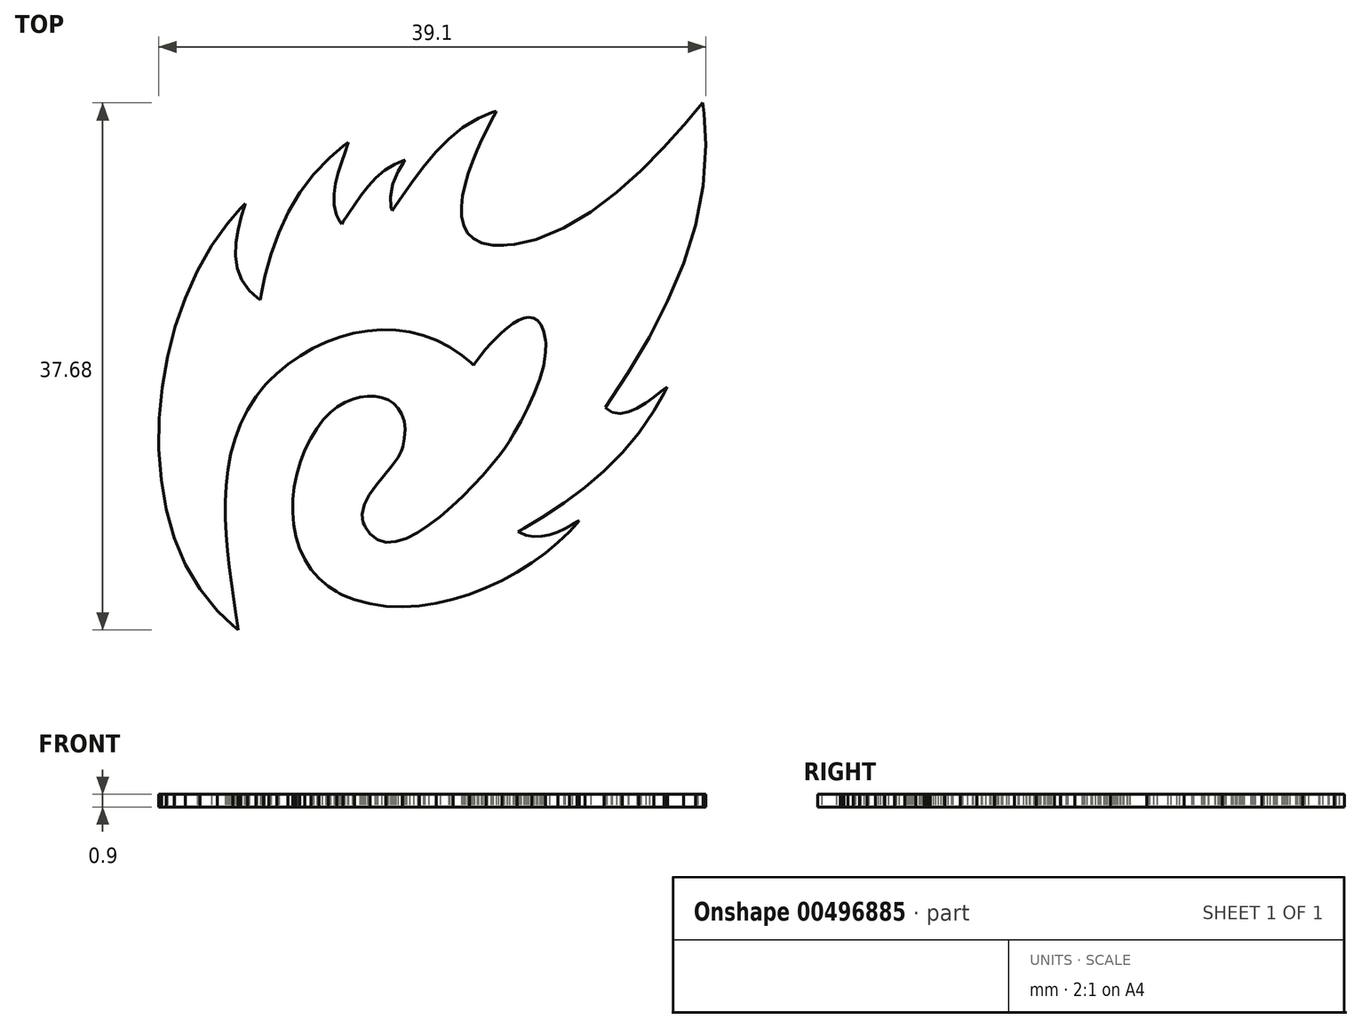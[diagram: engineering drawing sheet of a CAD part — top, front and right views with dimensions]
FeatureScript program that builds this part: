
annotation { "Feature Type Name" : "Feature", "Feature Type Description" : "" }
export const myFeature = defineFeature(function(context is Context, id is Id, definition is map)
    precondition{}
    {
        {
            var Q0;
            Q0=qCreatedBy(makeId("Top.planeOp"),FACE);
            var sketch = newSketch(context, id + "F0", { "sketchPlane" : qUnion([Q0])});
            skLineSegment(sketch, "E0", {"start": v(19.33, 18.84) * mm, "end": v(19.44, 18.1) * mm});
            skLineSegment(sketch, "E1", {"start": v(19.44, 18.1) * mm, "end": v(19.55, 15.84) * mm});
            skLineSegment(sketch, "E2", {"start": v(19.55, 15.84) * mm, "end": v(19.36, 12.93) * mm});
            skLineSegment(sketch, "E3", {"start": v(19.36, 12.93) * mm, "end": v(18.82, 10.1) * mm});
            skLineSegment(sketch, "E4", {"start": v(18.82, 10.1) * mm, "end": v(17.96, 7.36) * mm});
            skLineSegment(sketch, "E5", {"start": v(17.96, 7.36) * mm, "end": v(16.85, 4.69) * mm});
            skLineSegment(sketch, "E6", {"start": v(16.85, 4.69) * mm, "end": v(15.51, 2.09) * mm});
            skLineSegment(sketch, "E7", {"start": v(15.51, 2.09) * mm, "end": v(14.01, -0.45) * mm});
            skLineSegment(sketch, "E8", {"start": v(14.01, -0.45) * mm, "end": v(12.8, -2.31) * mm});
            skLineSegment(sketch, "E9", {"start": v(12.8, -2.31) * mm, "end": v(12.39, -2.92) * mm});
            skLineSegment(sketch, "E10", {"start": v(12.39, -2.92) * mm, "end": v(12.48, -3.04) * mm});
            skLineSegment(sketch, "E11", {"start": v(12.48, -3.04) * mm, "end": v(12.88, -3.29) * mm});
            skLineSegment(sketch, "E12", {"start": v(12.88, -3.29) * mm, "end": v(13.44, -3.38) * mm});
            skLineSegment(sketch, "E13", {"start": v(13.44, -3.38) * mm, "end": v(14.03, -3.26) * mm});
            skLineSegment(sketch, "E14", {"start": v(14.03, -3.26) * mm, "end": v(14.65, -2.99) * mm});
            skLineSegment(sketch, "E15", {"start": v(14.65, -2.99) * mm, "end": v(15.26, -2.61) * mm});
            skLineSegment(sketch, "E16", {"start": v(15.26, -2.61) * mm, "end": v(15.84, -2.2) * mm});
            skLineSegment(sketch, "E17", {"start": v(15.84, -2.2) * mm, "end": v(16.36, -1.8) * mm});
            skLineSegment(sketch, "E18", {"start": v(16.36, -1.8) * mm, "end": v(16.7, -1.54) * mm});
            skLineSegment(sketch, "E19", {"start": v(16.7, -1.54) * mm, "end": v(16.8, -1.46) * mm});
            skLineSegment(sketch, "E20", {"start": v(16.8, -1.46) * mm, "end": v(16.59, -1.9) * mm});
            skLineSegment(sketch, "E21", {"start": v(16.59, -1.9) * mm, "end": v(15.84, -3.2) * mm});
            skLineSegment(sketch, "E22", {"start": v(15.84, -3.2) * mm, "end": v(14.76, -4.76) * mm});
            skLineSegment(sketch, "E23", {"start": v(14.76, -4.76) * mm, "end": v(13.58, -6.18) * mm});
            skLineSegment(sketch, "E24", {"start": v(13.58, -6.18) * mm, "end": v(12.3, -7.47) * mm});
            skLineSegment(sketch, "E25", {"start": v(12.3, -7.47) * mm, "end": v(10.92, -8.65) * mm});
            skLineSegment(sketch, "E26", {"start": v(10.92, -8.65) * mm, "end": v(9.43, -9.76) * mm});
            skLineSegment(sketch, "E27", {"start": v(9.43, -9.76) * mm, "end": v(7.84, -10.8) * mm});
            skLineSegment(sketch, "E28", {"start": v(7.84, -10.8) * mm, "end": v(6.57, -11.58) * mm});
            skLineSegment(sketch, "E29", {"start": v(6.57, -11.58) * mm, "end": v(6.15, -11.82) * mm});
            skLineSegment(sketch, "E30", {"start": v(6.15, -11.82) * mm, "end": v(6.28, -11.9) * mm});
            skLineSegment(sketch, "E31", {"start": v(6.28, -11.9) * mm, "end": v(6.7, -12.06) * mm});
            skLineSegment(sketch, "E32", {"start": v(6.7, -12.06) * mm, "end": v(7.27, -12.17) * mm});
            skLineSegment(sketch, "E33", {"start": v(7.27, -12.17) * mm, "end": v(7.83, -12.15) * mm});
            skLineSegment(sketch, "E34", {"start": v(7.83, -12.15) * mm, "end": v(8.4, -12.03) * mm});
            skLineSegment(sketch, "E35", {"start": v(8.4, -12.03) * mm, "end": v(8.95, -11.84) * mm});
            skLineSegment(sketch, "E36", {"start": v(8.95, -11.84) * mm, "end": v(9.5, -11.59) * mm});
            skLineSegment(sketch, "E37", {"start": v(9.5, -11.59) * mm, "end": v(10.02, -11.3) * mm});
            skLineSegment(sketch, "E38", {"start": v(10.02, -11.3) * mm, "end": v(10.4, -11.09) * mm});
            skLineSegment(sketch, "E39", {"start": v(10.4, -11.09) * mm, "end": v(10.52, -11.02) * mm});
            skLineSegment(sketch, "E40", {"start": v(10.52, -11.02) * mm, "end": v(10.35, -11.22) * mm});
            skLineSegment(sketch, "E41", {"start": v(10.35, -11.22) * mm, "end": v(9.8, -11.82) * mm});
            skLineSegment(sketch, "E42", {"start": v(9.8, -11.82) * mm, "end": v(8.99, -12.6) * mm});
            skLineSegment(sketch, "E43", {"start": v(8.99, -12.6) * mm, "end": v(8.09, -13.34) * mm});
            skLineSegment(sketch, "E44", {"start": v(8.09, -13.34) * mm, "end": v(7.12, -14.04) * mm});
            skLineSegment(sketch, "E45", {"start": v(7.12, -14.04) * mm, "end": v(6.08, -14.7) * mm});
            skLineSegment(sketch, "E46", {"start": v(6.08, -14.7) * mm, "end": v(4.99, -15.3) * mm});
            skLineSegment(sketch, "E47", {"start": v(4.99, -15.3) * mm, "end": v(3.85, -15.83) * mm});
            skLineSegment(sketch, "E48", {"start": v(3.85, -15.83) * mm, "end": v(2.68, -16.29) * mm});
            skLineSegment(sketch, "E49", {"start": v(2.68, -16.29) * mm, "end": v(1.5, -16.66) * mm});
            skLineSegment(sketch, "E50", {"start": v(1.5, -16.66) * mm, "end": v(0.3, -16.94) * mm});
            skLineSegment(sketch, "E51", {"start": v(0.3, -16.94) * mm, "end": v(-0.91, -17.12) * mm});
            skLineSegment(sketch, "E52", {"start": v(-0.91, -17.12) * mm, "end": v(-2.11, -17.2) * mm});
            skLineSegment(sketch, "E53", {"start": v(-2.11, -17.2) * mm, "end": v(-3.3, -17.15) * mm});
            skLineSegment(sketch, "E54", {"start": v(-3.3, -17.15) * mm, "end": v(-4.44, -16.98) * mm});
            skLineSegment(sketch, "E55", {"start": v(-4.44, -16.98) * mm, "end": v(-5.56, -16.67) * mm});
            skLineSegment(sketch, "E56", {"start": v(-5.56, -16.67) * mm, "end": v(-6.37, -16.35) * mm});
            skLineSegment(sketch, "E57", {"start": v(-6.37, -16.35) * mm, "end": v(-6.62, -16.22) * mm});
            skLineSegment(sketch, "E58", {"start": v(-6.62, -16.22) * mm, "end": v(-6.83, -16.11) * mm});
            skLineSegment(sketch, "E59", {"start": v(-6.83, -16.11) * mm, "end": v(-7.41, -15.74) * mm});
            skLineSegment(sketch, "E60", {"start": v(-7.41, -15.74) * mm, "end": v(-8.1, -15.17) * mm});
            skLineSegment(sketch, "E61", {"start": v(-8.1, -15.17) * mm, "end": v(-8.66, -14.51) * mm});
            skLineSegment(sketch, "E62", {"start": v(-8.66, -14.51) * mm, "end": v(-9.12, -13.79) * mm});
            skLineSegment(sketch, "E63", {"start": v(-9.12, -13.79) * mm, "end": v(-9.48, -13) * mm});
            skLineSegment(sketch, "E64", {"start": v(-9.48, -13) * mm, "end": v(-9.74, -12.18) * mm});
            skLineSegment(sketch, "E65", {"start": v(-9.74, -12.18) * mm, "end": v(-9.9, -11.3) * mm});
            skLineSegment(sketch, "E66", {"start": v(-9.9, -11.3) * mm, "end": v(-9.97, -10.42) * mm});
            skLineSegment(sketch, "E67", {"start": v(-9.97, -10.42) * mm, "end": v(-9.96, -9.51) * mm});
            skLineSegment(sketch, "E68", {"start": v(-9.96, -9.51) * mm, "end": v(-9.86, -8.6) * mm});
            skLineSegment(sketch, "E69", {"start": v(-9.86, -8.6) * mm, "end": v(-9.68, -7.7) * mm});
            skLineSegment(sketch, "E70", {"start": v(-9.68, -7.7) * mm, "end": v(-9.43, -6.83) * mm});
            skLineSegment(sketch, "E71", {"start": v(-9.43, -6.83) * mm, "end": v(-9.1, -5.99) * mm});
            skLineSegment(sketch, "E72", {"start": v(-9.1, -5.99) * mm, "end": v(-8.71, -5.19) * mm});
            skLineSegment(sketch, "E73", {"start": v(-8.71, -5.19) * mm, "end": v(-8.25, -4.44) * mm});
            skLineSegment(sketch, "E74", {"start": v(-8.25, -4.44) * mm, "end": v(-7.87, -3.93) * mm});
            skLineSegment(sketch, "E75", {"start": v(-7.87, -3.93) * mm, "end": v(-7.74, -3.76) * mm});
            skLineSegment(sketch, "E76", {"start": v(-7.74, -3.76) * mm, "end": v(-7.63, -3.64) * mm});
            skLineSegment(sketch, "E77", {"start": v(-7.63, -3.64) * mm, "end": v(-7.28, -3.3) * mm});
            skLineSegment(sketch, "E78", {"start": v(-7.28, -3.3) * mm, "end": v(-6.78, -2.9) * mm});
            skLineSegment(sketch, "E79", {"start": v(-6.78, -2.9) * mm, "end": v(-6.25, -2.59) * mm});
            skLineSegment(sketch, "E80", {"start": v(-6.25, -2.59) * mm, "end": v(-5.7, -2.35) * mm});
            skLineSegment(sketch, "E81", {"start": v(-5.7, -2.35) * mm, "end": v(-5.16, -2.2) * mm});
            skLineSegment(sketch, "E82", {"start": v(-5.16, -2.2) * mm, "end": v(-4.62, -2.13) * mm});
            skLineSegment(sketch, "E83", {"start": v(-4.62, -2.13) * mm, "end": v(-4.1, -2.14) * mm});
            skLineSegment(sketch, "E84", {"start": v(-4.1, -2.14) * mm, "end": v(-3.6, -2.23) * mm});
            skLineSegment(sketch, "E85", {"start": v(-3.6, -2.23) * mm, "end": v(-3.15, -2.4) * mm});
            skLineSegment(sketch, "E86", {"start": v(-3.15, -2.4) * mm, "end": v(-2.76, -2.65) * mm});
            skLineSegment(sketch, "E87", {"start": v(-2.76, -2.65) * mm, "end": v(-2.43, -2.99) * mm});
            skLineSegment(sketch, "E88", {"start": v(-2.43, -2.99) * mm, "end": v(-2.17, -3.4) * mm});
            skLineSegment(sketch, "E89", {"start": v(-2.17, -3.4) * mm, "end": v(-2, -3.9) * mm});
            skLineSegment(sketch, "E90", {"start": v(-2, -3.9) * mm, "end": v(-1.94, -4.5) * mm});
            skLineSegment(sketch, "E91", {"start": v(-1.94, -4.5) * mm, "end": v(-2, -5.16) * mm});
            skLineSegment(sketch, "E92", {"start": v(-2, -5.16) * mm, "end": v(-2.1, -5.73) * mm});
            skLineSegment(sketch, "E93", {"start": v(-2.1, -5.73) * mm, "end": v(-2.16, -5.91) * mm});
            skLineSegment(sketch, "E94", {"start": v(-2.16, -5.91) * mm, "end": v(-2.21, -6.07) * mm});
            skLineSegment(sketch, "E95", {"start": v(-2.21, -6.07) * mm, "end": v(-2.45, -6.52) * mm});
            skLineSegment(sketch, "E96", {"start": v(-2.45, -6.52) * mm, "end": v(-2.9, -7.16) * mm});
            skLineSegment(sketch, "E97", {"start": v(-2.9, -7.16) * mm, "end": v(-3.45, -7.81) * mm});
            skLineSegment(sketch, "E98", {"start": v(-3.45, -7.81) * mm, "end": v(-4, -8.49) * mm});
            skLineSegment(sketch, "E99", {"start": v(-4, -8.49) * mm, "end": v(-4.5, -9.18) * mm});
            skLineSegment(sketch, "E100", {"start": v(-4.5, -9.18) * mm, "end": v(-4.86, -9.88) * mm});
            skLineSegment(sketch, "E101", {"start": v(-4.86, -9.88) * mm, "end": v(-5, -10.59) * mm});
            skLineSegment(sketch, "E102", {"start": v(-5, -10.59) * mm, "end": v(-4.94, -11.14) * mm});
            skLineSegment(sketch, "E103", {"start": v(-4.94, -11.14) * mm, "end": v(-4.87, -11.3) * mm});
            skLineSegment(sketch, "E104", {"start": v(-4.87, -11.3) * mm, "end": v(-4.79, -11.48) * mm});
            skLineSegment(sketch, "E105", {"start": v(-4.79, -11.48) * mm, "end": v(-4.44, -11.99) * mm});
            skLineSegment(sketch, "E106", {"start": v(-4.44, -11.99) * mm, "end": v(-3.91, -12.4) * mm});
            skLineSegment(sketch, "E107", {"start": v(-3.91, -12.4) * mm, "end": v(-3.29, -12.57) * mm});
            skLineSegment(sketch, "E108", {"start": v(-3.29, -12.57) * mm, "end": v(-2.6, -12.52) * mm});
            skLineSegment(sketch, "E109", {"start": v(-2.6, -12.52) * mm, "end": v(-1.84, -12.28) * mm});
            skLineSegment(sketch, "E110", {"start": v(-1.84, -12.28) * mm, "end": v(-1.05, -11.88) * mm});
            skLineSegment(sketch, "E111", {"start": v(-1.05, -11.88) * mm, "end": v(-0.24, -11.36) * mm});
            skLineSegment(sketch, "E112", {"start": v(-0.24, -11.36) * mm, "end": v(0.59, -10.73) * mm});
            skLineSegment(sketch, "E113", {"start": v(0.59, -10.73) * mm, "end": v(1.4, -10.02) * mm});
            skLineSegment(sketch, "E114", {"start": v(1.4, -10.02) * mm, "end": v(2.19, -9.28) * mm});
            skLineSegment(sketch, "E115", {"start": v(2.19, -9.28) * mm, "end": v(2.93, -8.52) * mm});
            skLineSegment(sketch, "E116", {"start": v(2.93, -8.52) * mm, "end": v(3.61, -7.77) * mm});
            skLineSegment(sketch, "E117", {"start": v(3.61, -7.77) * mm, "end": v(4.22, -7.07) * mm});
            skLineSegment(sketch, "E118", {"start": v(4.22, -7.07) * mm, "end": v(4.73, -6.44) * mm});
            skLineSegment(sketch, "E119", {"start": v(4.73, -6.44) * mm, "end": v(5.13, -5.92) * mm});
            skLineSegment(sketch, "E120", {"start": v(5.13, -5.92) * mm, "end": v(5.34, -5.62) * mm});
            skLineSegment(sketch, "E121", {"start": v(5.34, -5.62) * mm, "end": v(5.4, -5.52) * mm});
            skLineSegment(sketch, "E122", {"start": v(5.4, -5.52) * mm, "end": v(5.52, -5.34) * mm});
            skLineSegment(sketch, "E123", {"start": v(5.52, -5.34) * mm, "end": v(5.86, -4.78) * mm});
            skLineSegment(sketch, "E124", {"start": v(5.86, -4.78) * mm, "end": v(6.35, -3.92) * mm});
            skLineSegment(sketch, "E125", {"start": v(6.35, -3.92) * mm, "end": v(6.84, -2.97) * mm});
            skLineSegment(sketch, "E126", {"start": v(6.84, -2.97) * mm, "end": v(7.29, -1.97) * mm});
            skLineSegment(sketch, "E127", {"start": v(7.29, -1.97) * mm, "end": v(7.68, -0.95) * mm});
            skLineSegment(sketch, "E128", {"start": v(7.68, -0.95) * mm, "end": v(7.96, 0.06) * mm});
            skLineSegment(sketch, "E129", {"start": v(7.96, 0.06) * mm, "end": v(8.12, 1.01) * mm});
            skLineSegment(sketch, "E130", {"start": v(8.12, 1.01) * mm, "end": v(8.13, 1.66) * mm});
            skLineSegment(sketch, "E131", {"start": v(8.13, 1.66) * mm, "end": v(8.1, 1.87) * mm});
            skLineSegment(sketch, "E132", {"start": v(8.1, 1.87) * mm, "end": v(8.08, 2.03) * mm});
            skLineSegment(sketch, "E133", {"start": v(8.08, 2.03) * mm, "end": v(7.97, 2.5) * mm});
            skLineSegment(sketch, "E134", {"start": v(7.97, 2.5) * mm, "end": v(7.77, 2.97) * mm});
            skLineSegment(sketch, "E135", {"start": v(7.77, 2.97) * mm, "end": v(7.53, 3.28) * mm});
            skLineSegment(sketch, "E136", {"start": v(7.53, 3.28) * mm, "end": v(7.23, 3.46) * mm});
            skLineSegment(sketch, "E137", {"start": v(7.23, 3.46) * mm, "end": v(6.9, 3.5) * mm});
            skLineSegment(sketch, "E138", {"start": v(6.9, 3.5) * mm, "end": v(6.55, 3.45) * mm});
            skLineSegment(sketch, "E139", {"start": v(6.55, 3.45) * mm, "end": v(6.17, 3.3) * mm});
            skLineSegment(sketch, "E140", {"start": v(6.17, 3.3) * mm, "end": v(5.77, 3.06) * mm});
            skLineSegment(sketch, "E141", {"start": v(5.77, 3.06) * mm, "end": v(5.36, 2.77) * mm});
            skLineSegment(sketch, "E142", {"start": v(5.36, 2.77) * mm, "end": v(4.96, 2.42) * mm});
            skLineSegment(sketch, "E143", {"start": v(4.96, 2.42) * mm, "end": v(4.57, 2.03) * mm});
            skLineSegment(sketch, "E144", {"start": v(4.57, 2.03) * mm, "end": v(4.19, 1.63) * mm});
            skLineSegment(sketch, "E145", {"start": v(4.19, 1.63) * mm, "end": v(3.83, 1.21) * mm});
            skLineSegment(sketch, "E146", {"start": v(3.83, 1.21) * mm, "end": v(3.5, 0.8) * mm});
            skLineSegment(sketch, "E147", {"start": v(3.5, 0.8) * mm, "end": v(3.21, 0.43) * mm});
            skLineSegment(sketch, "E148", {"start": v(3.21, 0.43) * mm, "end": v(3.03, 0.17) * mm});
            skLineSegment(sketch, "E149", {"start": v(3.03, 0.17) * mm, "end": v(2.97, 0.08) * mm});
            skLineSegment(sketch, "E150", {"start": v(2.97, 0.08) * mm, "end": v(2.77, 0.27) * mm});
            skLineSegment(sketch, "E151", {"start": v(2.77, 0.27) * mm, "end": v(2.14, 0.8) * mm});
            skLineSegment(sketch, "E152", {"start": v(2.14, 0.8) * mm, "end": v(1.25, 1.4) * mm});
            skLineSegment(sketch, "E153", {"start": v(1.25, 1.4) * mm, "end": v(0.33, 1.86) * mm});
            skLineSegment(sketch, "E154", {"start": v(0.33, 1.86) * mm, "end": v(-0.63, 2.22) * mm});
            skLineSegment(sketch, "E155", {"start": v(-0.63, 2.22) * mm, "end": v(-1.6, 2.46) * mm});
            skLineSegment(sketch, "E156", {"start": v(-1.6, 2.46) * mm, "end": v(-2.6, 2.59) * mm});
            skLineSegment(sketch, "E157", {"start": v(-2.6, 2.59) * mm, "end": v(-3.62, 2.61) * mm});
            skLineSegment(sketch, "E158", {"start": v(-3.62, 2.61) * mm, "end": v(-4.63, 2.54) * mm});
            skLineSegment(sketch, "E159", {"start": v(-4.63, 2.54) * mm, "end": v(-5.63, 2.36) * mm});
            skLineSegment(sketch, "E160", {"start": v(-5.63, 2.36) * mm, "end": v(-6.62, 2.1) * mm});
            skLineSegment(sketch, "E161", {"start": v(-6.62, 2.1) * mm, "end": v(-7.6, 1.74) * mm});
            skLineSegment(sketch, "E162", {"start": v(-7.6, 1.74) * mm, "end": v(-8.53, 1.3) * mm});
            skLineSegment(sketch, "E163", {"start": v(-8.53, 1.3) * mm, "end": v(-9.44, 0.77) * mm});
            skLineSegment(sketch, "E164", {"start": v(-9.44, 0.77) * mm, "end": v(-10.3, 0.16) * mm});
            skLineSegment(sketch, "E165", {"start": v(-10.3, 0.16) * mm, "end": v(-11.1, -0.52) * mm});
            skLineSegment(sketch, "E166", {"start": v(-11.1, -0.52) * mm, "end": v(-11.68, -1.07) * mm});
            skLineSegment(sketch, "E167", {"start": v(-11.68, -1.07) * mm, "end": v(-11.86, -1.26) * mm});
            skLineSegment(sketch, "E168", {"start": v(-11.86, -1.26) * mm, "end": v(-12.06, -1.48) * mm});
            skLineSegment(sketch, "E169", {"start": v(-12.06, -1.48) * mm, "end": v(-12.6, -2.17) * mm});
            skLineSegment(sketch, "E170", {"start": v(-12.6, -2.17) * mm, "end": v(-13.21, -3.13) * mm});
            skLineSegment(sketch, "E171", {"start": v(-13.21, -3.13) * mm, "end": v(-13.71, -4.14) * mm});
            skLineSegment(sketch, "E172", {"start": v(-13.71, -4.14) * mm, "end": v(-14.1, -5.19) * mm});
            skLineSegment(sketch, "E173", {"start": v(-14.1, -5.19) * mm, "end": v(-14.4, -6.27) * mm});
            skLineSegment(sketch, "E174", {"start": v(-14.4, -6.27) * mm, "end": v(-14.6, -7.39) * mm});
            skLineSegment(sketch, "E175", {"start": v(-14.6, -7.39) * mm, "end": v(-14.73, -8.53) * mm});
            skLineSegment(sketch, "E176", {"start": v(-14.73, -8.53) * mm, "end": v(-14.79, -9.68) * mm});
            skLineSegment(sketch, "E177", {"start": v(-14.79, -9.68) * mm, "end": v(-14.79, -10.85) * mm});
            skLineSegment(sketch, "E178", {"start": v(-14.79, -10.85) * mm, "end": v(-14.73, -12.02) * mm});
            skLineSegment(sketch, "E179", {"start": v(-14.73, -12.02) * mm, "end": v(-14.64, -13.2) * mm});
            skLineSegment(sketch, "E180", {"start": v(-14.64, -13.2) * mm, "end": v(-14.51, -14.36) * mm});
            skLineSegment(sketch, "E181", {"start": v(-14.51, -14.36) * mm, "end": v(-14.36, -15.51) * mm});
            skLineSegment(sketch, "E182", {"start": v(-14.36, -15.51) * mm, "end": v(-14.2, -16.65) * mm});
            skLineSegment(sketch, "E183", {"start": v(-14.2, -16.65) * mm, "end": v(-14.03, -17.76) * mm});
            skLineSegment(sketch, "E184", {"start": v(-14.03, -17.76) * mm, "end": v(-13.9, -18.57) * mm});
            skLineSegment(sketch, "E185", {"start": v(-13.9, -18.57) * mm, "end": v(-13.86, -18.84) * mm});
            skLineSegment(sketch, "E186", {"start": v(-13.86, -18.84) * mm, "end": v(-14.26, -18.53) * mm});
            skLineSegment(sketch, "E187", {"start": v(-14.26, -18.53) * mm, "end": v(-15.36, -17.48) * mm});
            skLineSegment(sketch, "E188", {"start": v(-15.36, -17.48) * mm, "end": v(-16.61, -15.91) * mm});
            skLineSegment(sketch, "E189", {"start": v(-16.61, -15.91) * mm, "end": v(-17.64, -14.16) * mm});
            skLineSegment(sketch, "E190", {"start": v(-17.64, -14.16) * mm, "end": v(-18.43, -12.26) * mm});
            skLineSegment(sketch, "E191", {"start": v(-18.43, -12.26) * mm, "end": v(-19.01, -10.23) * mm});
            skLineSegment(sketch, "E192", {"start": v(-19.01, -10.23) * mm, "end": v(-19.38, -8.11) * mm});
            skLineSegment(sketch, "E193", {"start": v(-19.38, -8.11) * mm, "end": v(-19.55, -5.93) * mm});
            skLineSegment(sketch, "E194", {"start": v(-19.55, -5.93) * mm, "end": v(-19.52, -3.72) * mm});
            skLineSegment(sketch, "E195", {"start": v(-19.52, -3.72) * mm, "end": v(-19.31, -1.5) * mm});
            skLineSegment(sketch, "E196", {"start": v(-19.31, -1.5) * mm, "end": v(-18.93, 0.7) * mm});
            skLineSegment(sketch, "E197", {"start": v(-18.93, 0.7) * mm, "end": v(-18.37, 2.83) * mm});
            skLineSegment(sketch, "E198", {"start": v(-18.37, 2.83) * mm, "end": v(-17.66, 4.89) * mm});
            skLineSegment(sketch, "E199", {"start": v(-17.66, 4.89) * mm, "end": v(-16.8, 6.82) * mm});
            skLineSegment(sketch, "E200", {"start": v(-16.8, 6.82) * mm, "end": v(-15.78, 8.61) * mm});
            skLineSegment(sketch, "E201", {"start": v(-15.78, 8.61) * mm, "end": v(-14.64, 10.23) * mm});
            skLineSegment(sketch, "E202", {"start": v(-14.64, 10.23) * mm, "end": v(-13.7, 11.3) * mm});
            skLineSegment(sketch, "E203", {"start": v(-13.7, 11.3) * mm, "end": v(-13.37, 11.64) * mm});
            skLineSegment(sketch, "E204", {"start": v(-13.37, 11.64) * mm, "end": v(-13.44, 11.41) * mm});
            skLineSegment(sketch, "E205", {"start": v(-13.44, 11.41) * mm, "end": v(-13.65, 10.72) * mm});
            skLineSegment(sketch, "E206", {"start": v(-13.65, 10.72) * mm, "end": v(-13.87, 9.78) * mm});
            skLineSegment(sketch, "E207", {"start": v(-13.87, 9.78) * mm, "end": v(-14.02, 8.84) * mm});
            skLineSegment(sketch, "E208", {"start": v(-14.02, 8.84) * mm, "end": v(-14.05, 7.9) * mm});
            skLineSegment(sketch, "E209", {"start": v(-14.05, 7.9) * mm, "end": v(-13.92, 7.02) * mm});
            skLineSegment(sketch, "E210", {"start": v(-13.92, 7.02) * mm, "end": v(-13.6, 6.18) * mm});
            skLineSegment(sketch, "E211", {"start": v(-13.6, 6.18) * mm, "end": v(-13.07, 5.42) * mm});
            skLineSegment(sketch, "E212", {"start": v(-13.07, 5.42) * mm, "end": v(-12.5, 4.9) * mm});
            skLineSegment(sketch, "E213", {"start": v(-12.5, 4.9) * mm, "end": v(-12.28, 4.76) * mm});
            skLineSegment(sketch, "E214", {"start": v(-12.28, 4.76) * mm, "end": v(-12.21, 5.18) * mm});
            skLineSegment(sketch, "E215", {"start": v(-12.21, 5.18) * mm, "end": v(-11.95, 6.42) * mm});
            skLineSegment(sketch, "E216", {"start": v(-11.95, 6.42) * mm, "end": v(-11.52, 8.03) * mm});
            skLineSegment(sketch, "E217", {"start": v(-11.52, 8.03) * mm, "end": v(-10.96, 9.58) * mm});
            skLineSegment(sketch, "E218", {"start": v(-10.96, 9.58) * mm, "end": v(-10.28, 11.05) * mm});
            skLineSegment(sketch, "E219", {"start": v(-10.28, 11.05) * mm, "end": v(-9.45, 12.44) * mm});
            skLineSegment(sketch, "E220", {"start": v(-9.45, 12.44) * mm, "end": v(-8.47, 13.74) * mm});
            skLineSegment(sketch, "E221", {"start": v(-8.47, 13.74) * mm, "end": v(-7.32, 14.93) * mm});
            skLineSegment(sketch, "E222", {"start": v(-7.32, 14.93) * mm, "end": v(-6.33, 15.76) * mm});
            skLineSegment(sketch, "E223", {"start": v(-6.33, 15.76) * mm, "end": v(-5.99, 16) * mm});
            skLineSegment(sketch, "E224", {"start": v(-5.99, 16) * mm, "end": v(-6.05, 15.84) * mm});
            skLineSegment(sketch, "E225", {"start": v(-6.05, 15.84) * mm, "end": v(-6.23, 15.33) * mm});
            skLineSegment(sketch, "E226", {"start": v(-6.23, 15.33) * mm, "end": v(-6.49, 14.6) * mm});
            skLineSegment(sketch, "E227", {"start": v(-6.49, 14.6) * mm, "end": v(-6.73, 13.85) * mm});
            skLineSegment(sketch, "E228", {"start": v(-6.73, 13.85) * mm, "end": v(-6.92, 13.07) * mm});
            skLineSegment(sketch, "E229", {"start": v(-6.92, 13.07) * mm, "end": v(-7.02, 12.3) * mm});
            skLineSegment(sketch, "E230", {"start": v(-7.02, 12.3) * mm, "end": v(-7, 11.56) * mm});
            skLineSegment(sketch, "E231", {"start": v(-7, 11.56) * mm, "end": v(-6.84, 10.84) * mm});
            skLineSegment(sketch, "E232", {"start": v(-6.84, 10.84) * mm, "end": v(-6.6, 10.33) * mm});
            skLineSegment(sketch, "E233", {"start": v(-6.6, 10.33) * mm, "end": v(-6.49, 10.18) * mm});
            skLineSegment(sketch, "E234", {"start": v(-6.49, 10.18) * mm, "end": v(-6.37, 10.35) * mm});
            skLineSegment(sketch, "E235", {"start": v(-6.37, 10.35) * mm, "end": v(-6.03, 10.86) * mm});
            skLineSegment(sketch, "E236", {"start": v(-6.03, 10.86) * mm, "end": v(-5.56, 11.55) * mm});
            skLineSegment(sketch, "E237", {"start": v(-5.56, 11.55) * mm, "end": v(-5.08, 12.23) * mm});
            skLineSegment(sketch, "E238", {"start": v(-5.08, 12.23) * mm, "end": v(-4.57, 12.89) * mm});
            skLineSegment(sketch, "E239", {"start": v(-4.57, 12.89) * mm, "end": v(-4.01, 13.5) * mm});
            skLineSegment(sketch, "E240", {"start": v(-4.01, 13.5) * mm, "end": v(-3.4, 14.02) * mm});
            skLineSegment(sketch, "E241", {"start": v(-3.4, 14.02) * mm, "end": v(-2.7, 14.45) * mm});
            skLineSegment(sketch, "E242", {"start": v(-2.7, 14.45) * mm, "end": v(-2.12, 14.7) * mm});
            skLineSegment(sketch, "E243", {"start": v(-2.12, 14.7) * mm, "end": v(-1.92, 14.76) * mm});
            skLineSegment(sketch, "E244", {"start": v(-1.92, 14.76) * mm, "end": v(-2.07, 14.56) * mm});
            skLineSegment(sketch, "E245", {"start": v(-2.07, 14.56) * mm, "end": v(-2.45, 13.93) * mm});
            skLineSegment(sketch, "E246", {"start": v(-2.45, 13.93) * mm, "end": v(-2.82, 13.04) * mm});
            skLineSegment(sketch, "E247", {"start": v(-2.82, 13.04) * mm, "end": v(-2.98, 12.11) * mm});
            skLineSegment(sketch, "E248", {"start": v(-2.98, 12.11) * mm, "end": v(-2.93, 11.38) * mm});
            skLineSegment(sketch, "E249", {"start": v(-2.93, 11.38) * mm, "end": v(-2.87, 11.14) * mm});
            skLineSegment(sketch, "E250", {"start": v(-2.87, 11.14) * mm, "end": v(-2.67, 11.41) * mm});
            skLineSegment(sketch, "E251", {"start": v(-2.67, 11.41) * mm, "end": v(-2.08, 12.24) * mm});
            skLineSegment(sketch, "E252", {"start": v(-2.08, 12.24) * mm, "end": v(-1.32, 13.32) * mm});
            skLineSegment(sketch, "E253", {"start": v(-1.32, 13.32) * mm, "end": v(-0.54, 14.36) * mm});
            skLineSegment(sketch, "E254", {"start": v(-0.54, 14.36) * mm, "end": v(0.28, 15.35) * mm});
            skLineSegment(sketch, "E255", {"start": v(0.28, 15.35) * mm, "end": v(1.17, 16.26) * mm});
            skLineSegment(sketch, "E256", {"start": v(1.17, 16.26) * mm, "end": v(2.17, 17.06) * mm});
            skLineSegment(sketch, "E257", {"start": v(2.17, 17.06) * mm, "end": v(3.3, 17.73) * mm});
            skLineSegment(sketch, "E258", {"start": v(3.3, 17.73) * mm, "end": v(4.25, 18.14) * mm});
            skLineSegment(sketch, "E259", {"start": v(4.25, 18.14) * mm, "end": v(4.58, 18.24) * mm});
            skLineSegment(sketch, "E260", {"start": v(4.58, 18.24) * mm, "end": v(4.5, 18.1) * mm});
            skLineSegment(sketch, "E261", {"start": v(4.5, 18.1) * mm, "end": v(4.27, 17.65) * mm});
            skLineSegment(sketch, "E262", {"start": v(4.27, 17.65) * mm, "end": v(3.93, 16.98) * mm});
            skLineSegment(sketch, "E263", {"start": v(3.93, 16.98) * mm, "end": v(3.57, 16.25) * mm});
            skLineSegment(sketch, "E264", {"start": v(3.57, 16.25) * mm, "end": v(3.22, 15.46) * mm});
            skLineSegment(sketch, "E265", {"start": v(3.22, 15.46) * mm, "end": v(2.89, 14.64) * mm});
            skLineSegment(sketch, "E266", {"start": v(2.89, 14.64) * mm, "end": v(2.59, 13.82) * mm});
            skLineSegment(sketch, "E267", {"start": v(2.59, 13.82) * mm, "end": v(2.34, 13) * mm});
            skLineSegment(sketch, "E268", {"start": v(2.34, 13) * mm, "end": v(2.17, 12.19) * mm});
            skLineSegment(sketch, "E269", {"start": v(2.17, 12.19) * mm, "end": v(2.09, 11.43) * mm});
            skLineSegment(sketch, "E270", {"start": v(2.09, 11.43) * mm, "end": v(2.1, 10.72) * mm});
            skLineSegment(sketch, "E271", {"start": v(2.1, 10.72) * mm, "end": v(2.25, 10.1) * mm});
            skLineSegment(sketch, "E272", {"start": v(2.25, 10.1) * mm, "end": v(2.53, 9.55) * mm});
            skLineSegment(sketch, "E273", {"start": v(2.53, 9.55) * mm, "end": v(2.96, 9.12) * mm});
            skLineSegment(sketch, "E274", {"start": v(2.96, 9.12) * mm, "end": v(3.57, 8.82) * mm});
            skLineSegment(sketch, "E275", {"start": v(3.57, 8.82) * mm, "end": v(4.37, 8.67) * mm});
            skLineSegment(sketch, "E276", {"start": v(4.37, 8.67) * mm, "end": v(5.12, 8.65) * mm});
            skLineSegment(sketch, "E277", {"start": v(5.12, 8.65) * mm, "end": v(5.37, 8.67) * mm});
            skLineSegment(sketch, "E278", {"start": v(5.37, 8.67) * mm, "end": v(5.89, 8.72) * mm});
            skLineSegment(sketch, "E279", {"start": v(5.89, 8.72) * mm, "end": v(7.42, 9.08) * mm});
            skLineSegment(sketch, "E280", {"start": v(7.42, 9.08) * mm, "end": v(9.42, 9.9) * mm});
            skLineSegment(sketch, "E281", {"start": v(9.42, 9.9) * mm, "end": v(11.34, 11.03) * mm});
            skLineSegment(sketch, "E282", {"start": v(11.34, 11.03) * mm, "end": v(13.18, 12.42) * mm});
            skLineSegment(sketch, "E283", {"start": v(13.18, 12.42) * mm, "end": v(14.91, 13.98) * mm});
            skLineSegment(sketch, "E284", {"start": v(14.91, 13.98) * mm, "end": v(16.53, 15.62) * mm});
            skLineSegment(sketch, "E285", {"start": v(16.53, 15.62) * mm, "end": v(18, 17.27) * mm});
            skLineSegment(sketch, "E286", {"start": v(18, 17.27) * mm, "end": v(19, 18.44) * mm});
            skLineSegment(sketch, "E287", {"start": v(19, 18.44) * mm, "end": v(19.33, 18.84) * mm});
            skSolve(sketch);
        }
        {
            var Q0;
            Q0 = qSketchRegion(id + "F0", true);
            extrude(context, id + "F1", {"entities" : qUnion([Q0]), "depth" : .9 * mm});
        }
    });
